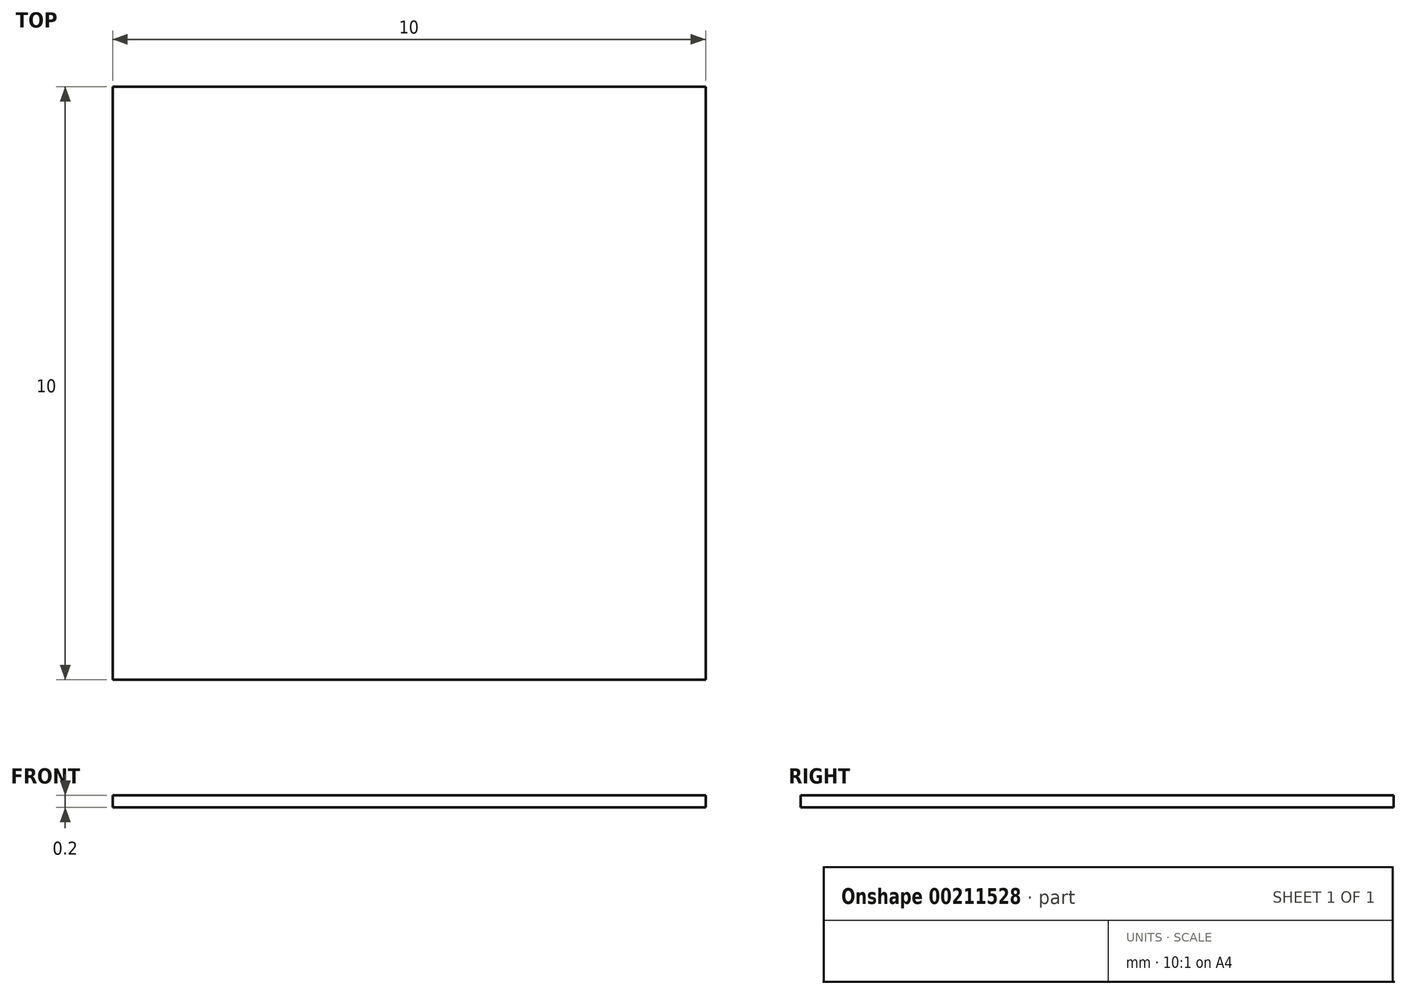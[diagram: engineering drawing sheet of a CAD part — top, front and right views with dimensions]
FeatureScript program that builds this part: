
annotation { "Feature Type Name" : "Feature", "Feature Type Description" : "" }
export const myFeature = defineFeature(function(context is Context, id is Id, definition is map)
    precondition{}
    {
        {
            var Q0;
            Q0=qCreatedBy(makeId("Top.planeOp"),FACE);
            var sketch = newSketch(context, id + "F0", { "sketchPlane" : qUnion([Q0])});
            skLineSegment(sketch, "E0.bottom", {"start": v(5, 5) * mm, "end": v(-5, 5) * mm});
            skLineSegment(sketch, "E0.top", {"start": v(5, -5) * mm, "end": v(-5, -5) * mm});
            skLineSegment(sketch, "E0.left", {"start": v(5, 5) * mm, "end": v(5, -5) * mm});
            skLineSegment(sketch, "E0.right", {"start": v(-5, 5) * mm, "end": v(-5, -5) * mm});
            skPoint(sketch, "E0.middle", {"position": v(0, 0) * mm});
            skSolve(sketch);
        }
        {
            var Q0;
            Q0 = qSketchRegion(id + "F0", true);
            extrude(context, id + "F1", {"entities" : qUnion([Q0]), "depth" : 0.2 * mm});
        }
    });
